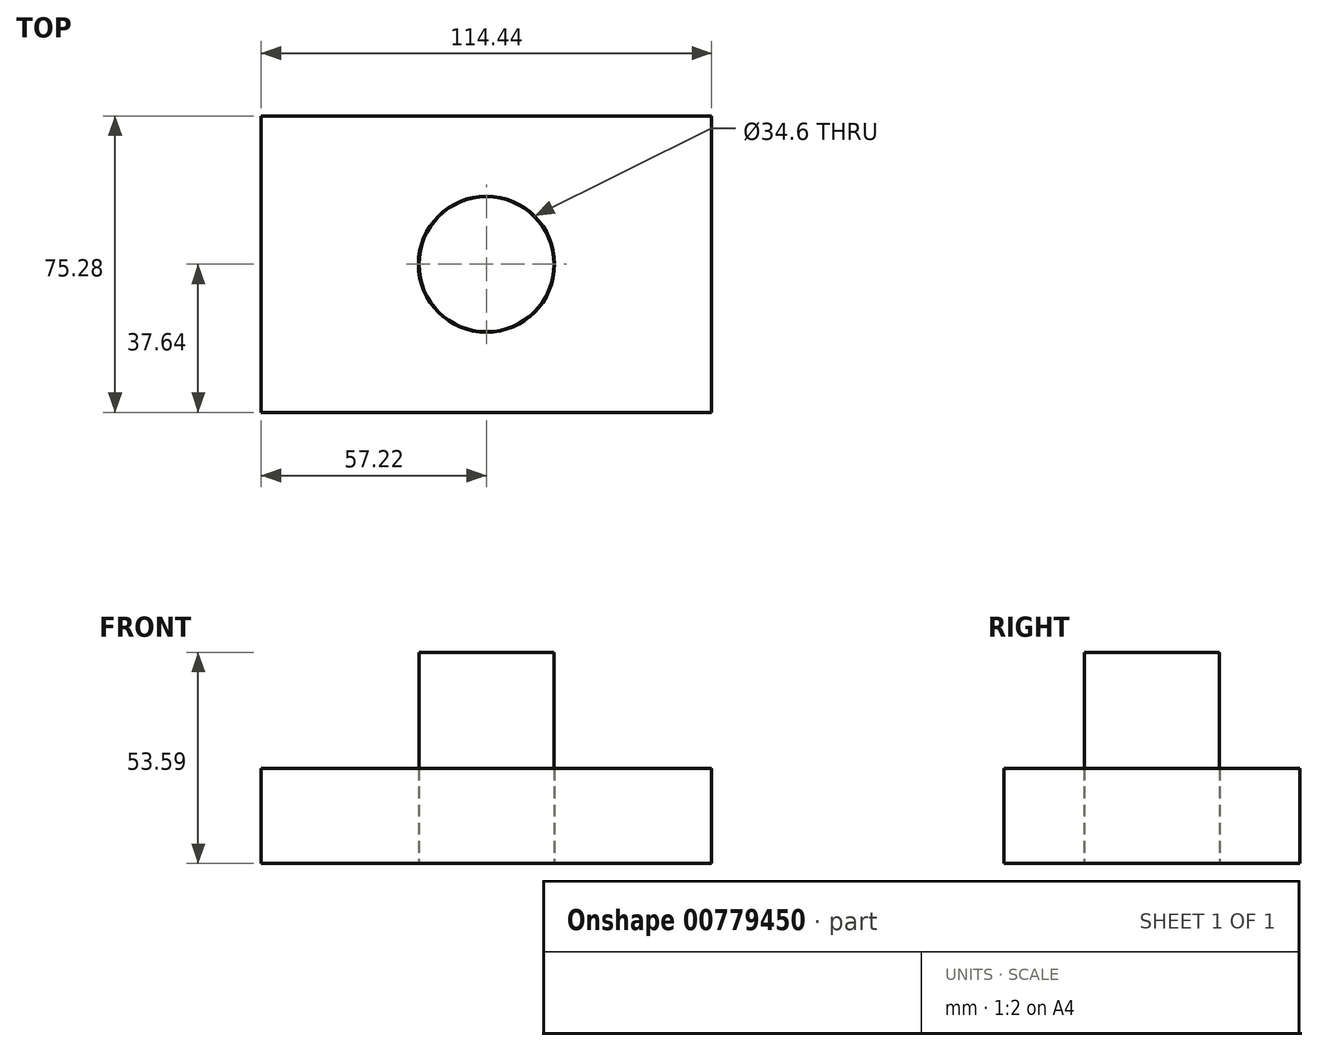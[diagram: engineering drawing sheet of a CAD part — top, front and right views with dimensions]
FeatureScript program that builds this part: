
annotation { "Feature Type Name" : "Feature", "Feature Type Description" : "" }
export const myFeature = defineFeature(function(context is Context, id is Id, definition is map)
    precondition{}
    {
        {
            var Q0;
            Q0=qCreatedBy(makeId("Top.planeOp"),FACE);
            var sketch = newSketch(context, id + "F0", { "sketchPlane" : qUnion([Q0])});
            skLineSegment(sketch, "E0.bottom", {"start": v(-57.22, 37.64) * mm, "end": v(57.22, 37.64) * mm});
            skLineSegment(sketch, "E0.top", {"start": v(-57.22, -37.64) * mm, "end": v(57.22, -37.64) * mm});
            skLineSegment(sketch, "E0.left", {"start": v(-57.22, 37.64) * mm, "end": v(-57.22, -37.64) * mm});
            skLineSegment(sketch, "E0.right", {"start": v(57.22, 37.64) * mm, "end": v(57.22, -37.64) * mm});
            skPoint(sketch, "E0.middle", {"position": v(0, 0) * mm});
            skCircle(sketch, "E1", {"center": v(0, 0) * mm, "radius": 17.3 * mm});
            skSolve(sketch);
        }
        {
            var Q0;
            Q0=makeQuery(id+"F0.imprint","IMPRINT",FACE,{"disambiguationData":[TD([[makeQuery(id+"F0.imprint","IMPRINT",EDGE,{"derivedFrom":sQuery(id+"F0.wireOp",EDGE,"E0.bottom")}),-1.0]])]});
            extrude(context, id + "F1", {"entities" : qUnion([Q0]), "depth" : 24.13 * mm, "offsetDistance" : 25.4 * mm});
        }
        {
            var Q0;
            Q0=qCreatedBy(makeId("Top.planeOp"),FACE);
            var sketch = newSketch(context, id + "F2", { "sketchPlane" : qUnion([Q0])});
            skCircle(sketch, "E2", {"center": v(0, 0) * mm, "radius": 17.14 * mm});
            skSolve(sketch);
        }
        {
            var Q0;
            Q0=makeQuery(id+"F2.imprint","IMPRINT",FACE,{"disambiguationData":[TD([[makeQuery(id+"F2.imprint","IMPRINT",EDGE,{"derivedFrom":sQuery(id+"F2.wireOp",EDGE,"E2")}),1.0]])]});
            extrude(context, id + "F3", {"entities" : qUnion([Q0]), "depth" : 53.6 * mm, "offsetDistance" : 25.4 * mm});
        }
    });
